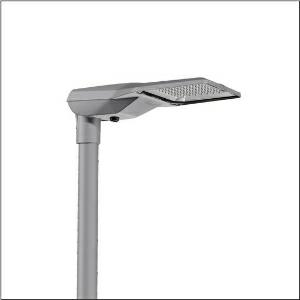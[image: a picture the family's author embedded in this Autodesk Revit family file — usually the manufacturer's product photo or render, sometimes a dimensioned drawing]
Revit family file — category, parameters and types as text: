
# Revit family: streetlight_sl_21_midi___p0_5a_5xe3v33r08nb_a07d
name_source: partatom
category: Lighting Fixtures
units: mm (PartAtom-declared; Revit-internal decimal feet)

## family parameters
Cut with Voids When Loaded = No
Host = Face
Light Source = No
Part Type = Normal
Room Calculation Point = No
Round Connector Dimension = Use Diameter
Shared = No

## types (1)
- --- (1 x LED, 22310 lm, 151.2 W, 3000K)
    Apparent Load = 151 VA
    CIE Flux Codes = 37 73 96 100 100
    Color Rendering = 70
    Color Temperature = 3000K
    Default Elevation = 1800 mm
    Description = Streetlight SL 21 midi, mast luminaire, primary light control with lens, of PMMA, primary optical cover: cover, of toughened safety glass, transparent, light distribution: P0.5a, light emission: direct distribution, primary light characteristic: asymmetric, installation type: post-top, side-entry, LED, High Power LED, rated luminous flux: 22.310lm, luminous efficacy: 148lm/W, light colour: 730, colour temperature: 3000K, control gear: D4i, control: pre-setting: logarithmic dimming characteristic, flexible luminous flux parameterisation, time-dependent luminous flux control, constant luminous flux control, overheat protection, mains connection: 230..240V, AC, 50/60Hz, start of lifetime: 151W, end of service life: 157W, reduction: 70W, luminaire housing, of diecast aluminium, powder-coated, Siteco® metallic grey (DB 702S), corrosivity category C5 mid according to DIN EN ISO 12944, multi-level sealing system, sealing non-destructively replaceable, inclination adjustable: 0°, 5°, 10°, 15°, please order mast flange separately, length: 644mm, width: 335mm, height: 110mm, mast flange for spigot size: 42mm (side-entry): 5XC10008XM4, 60/48mm (side-entry/post-top): 5XC10108XM2, 76/60mm (side-entry/post-top): 5XC10108XM1, mounting height: 4..8m, Smart Interface below, protection rating (complete): IP66, insulation class (complete): insulation class II (safety insulation), certification: CE, ENEC, ENEC+, VDE, impact resistance: IK10, permissible operating ambient temperature for outdoor applications: -40..+50°C, standard-compliant lighting for roads and squares, packaging unit: 1 piece

Light Distribution: P0.5a
    Height = 111 mm
    Lamp = 1 x LED
    Lamp Light Flux = 22310 lm
    Lamp Power = 151.2 W
    Lamp count = 1
    Length = 644 mm
    Luminous efficacy = 148 lm/W
    Manufacturer = Siteco
    ModVariant = No
    Model = 5XE3V33R08NB
    Number of Poles = 1
    OnlyDefault = Yes
    Power Factor = 1
    Product Name = Streetlight SL 21 midi | P0.5a
    Product group = mast luminaire | pylon top
    ProductGroupID = 6100
    Protection Class = Protection class II
    Protection Degree = IP 66
    RLX_Detail_Level = 1
    RLX_Emergency_Light_Flux = 0 lm
    RLX_Emergency_Type = 0
    RLX_Emergency_Type_DB = No
    RlxData = <blob elided: 26781 chars, md5=3b15c031>
    Socket = socket
    Standby Power = 0 W
    System Light Flux = 22310 lm
    System Power = 151 W
    Type Comments = factory setting: luminous flux: 100 % | dim-lin: 254 | 802 mA
    Type Image = l_1004300.jpg
    URL = http://relux.com
    VarID = @adj_069080
    Voltage = 0 V
    Weight = 0.00 kg
    Width = 336 mm

## geometry (parser evidence)
native form markers: Blend x4, Sweep x13
no freeform markers — native parametric forms only
